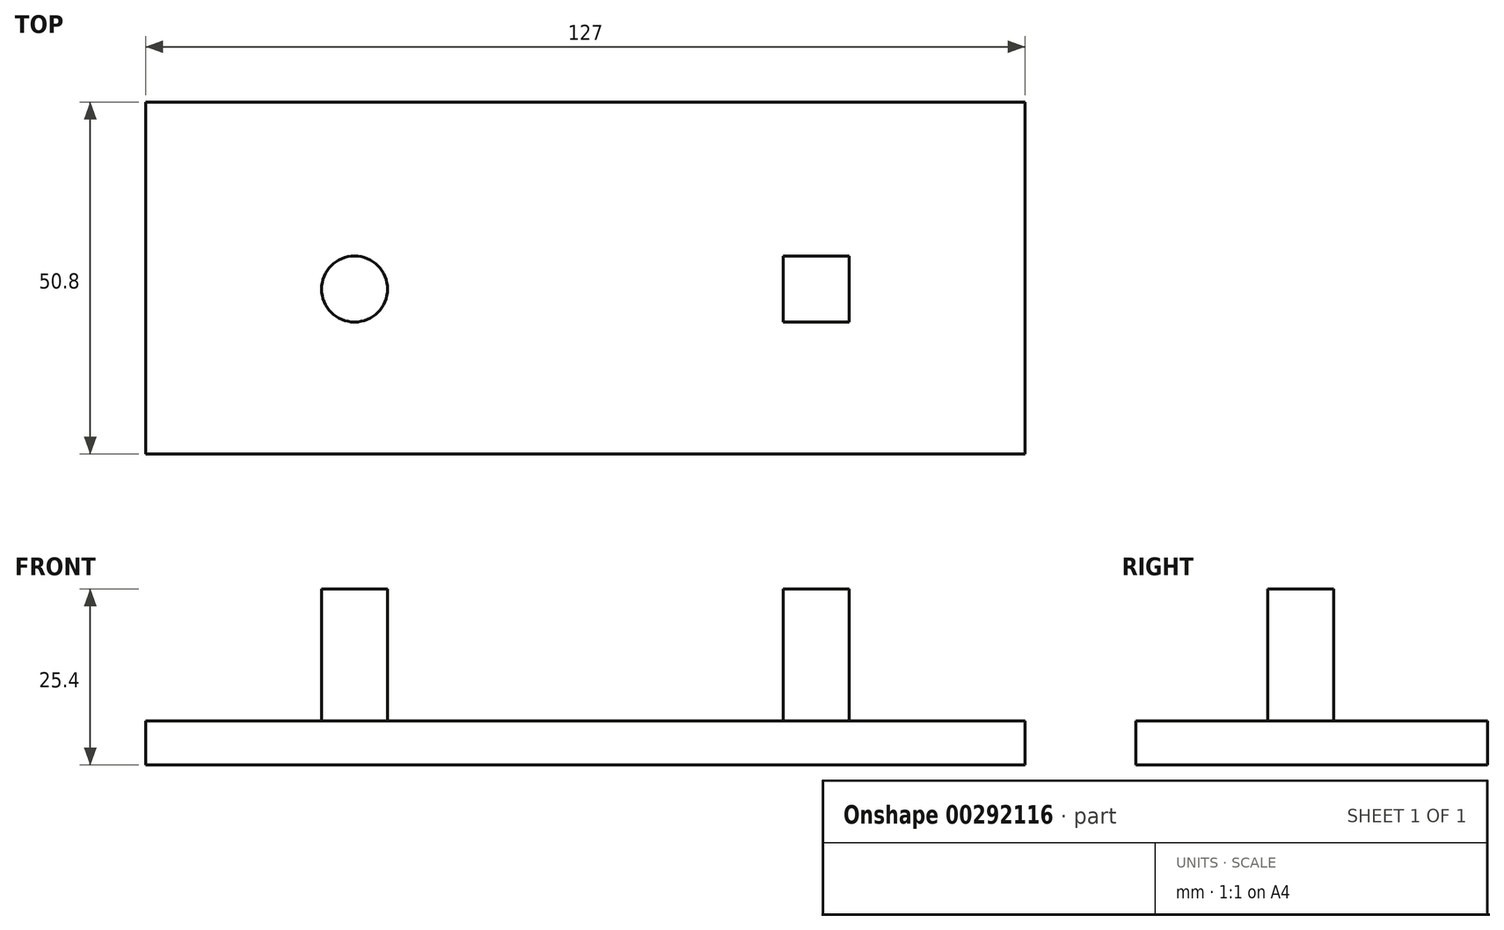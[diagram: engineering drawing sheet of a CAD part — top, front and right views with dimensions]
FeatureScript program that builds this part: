
annotation { "Feature Type Name" : "Feature", "Feature Type Description" : "" }
export const myFeature = defineFeature(function(context is Context, id is Id, definition is map)
    precondition{}
    {
        {
            var Q0;
            Q0=qCreatedBy(makeId("Top.planeOp"),FACE);
            var sketch = newSketch(context, id + "F0", { "sketchPlane" : qUnion([Q0])});
            skLineSegment(sketch, "E0.bottom", {"start": v(63.5, 25.4) * mm, "end": v(-63.5, 25.4) * mm});
            skLineSegment(sketch, "E0.top", {"start": v(63.5, -25.4) * mm, "end": v(-63.5, -25.4) * mm});
            skLineSegment(sketch, "E0.left", {"start": v(63.5, 25.4) * mm, "end": v(63.5, -25.4) * mm});
            skLineSegment(sketch, "E0.right", {"start": v(-63.5, 25.4) * mm, "end": v(-63.5, -25.4) * mm});
            skPoint(sketch, "E0.middle", {"position": v(0, 0) * mm});
            skLineSegment(sketch, "E1.bottom", {"start": v(38.1, 3.17) * mm, "end": v(28.58, 3.17) * mm});
            skLineSegment(sketch, "E1.top", {"start": v(38.1, -6.35) * mm, "end": v(28.58, -6.35) * mm});
            skLineSegment(sketch, "E1.left", {"start": v(38.1, 3.17) * mm, "end": v(38.1, -6.35) * mm});
            skLineSegment(sketch, "E1.right", {"start": v(28.58, 3.17) * mm, "end": v(28.58, -6.35) * mm});
            skCircle(sketch, "E2", {"center": v(-33.34, -1.59) * mm, "radius": 4.76 * mm});
            skSolve(sketch);
        }
        {
            var Q0;
            Q0=makeQuery(id+"F0.imprint","IMPRINT",FACE,{"disambiguationData":[TD([[makeQuery(id+"F0.imprint","IMPRINT",EDGE,{"derivedFrom":sQuery(id+"F0.wireOp",EDGE,"E0.bottom")}),1.0]])]});
            extrude(context, id + "F1", {"entities" : qUnion([Q0]), "depth" : 6.35 * mm});
        }
        {
            var Q0;
            Q0=makeQuery(id+"F0.imprint","IMPRINT",FACE,{"disambiguationData":[TD([[makeQuery(id+"F0.imprint","IMPRINT",EDGE,{"derivedFrom":sQuery(id+"F0.wireOp",EDGE,"E1.bottom")}),1.0]])]});
            var Q1;
            Q1=makeQuery(id+"F0.imprint","IMPRINT",FACE,{"disambiguationData":[TD([[makeQuery(id+"F0.imprint","IMPRINT",EDGE,{"derivedFrom":sQuery(id+"F0.wireOp",EDGE,"E2")}),1.0]])]});
            extrude(context, id + "F2", {"entities" : qUnion([Q0, Q1]), "operationType" : NewBodyOperationType.ADD, "depth" : 25.4 * mm});
        }
    });
